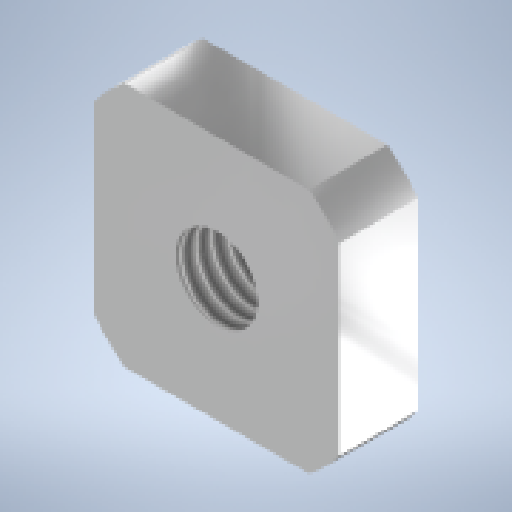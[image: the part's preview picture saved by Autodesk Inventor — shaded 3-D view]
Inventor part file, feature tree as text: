
AUTODESK INVENTOR PART (.ipt)
format: ipt  version: 2024 (Build 280153000, 153)  size: 232,448 bytes
history: native  units: mm
features: sketch x2, extrude x1, hole x1
ambient origin geometry x8: Origin, YZ Plane, XZ Plane, XY Plane, X Axis, Y Axis, Z Axis, Center Point
bodies: Solid1 (feature_tree)
feature tree (4):
  extrude  "Extrusion1"  Depth=20.0mm
  hole  "Hole1"  [1 undecoded]
  sketch  "Sketch1"  dims[d0=25.0mm d1=20.0mm]
  sketch  "Sketch2"  dims[d2=6.35mm d3=0.0mm d4=6.647mm d5=16.0mm d6=4.0mm d7=2.0mm d8=90.0deg d9=8.0mm d10=20.594885mm]
note: 1 required parameter value undecoded (feature->parameter linkage not recoverable at this tier; creation-order binding heuristic only, values carry confidence <= 0.55)
